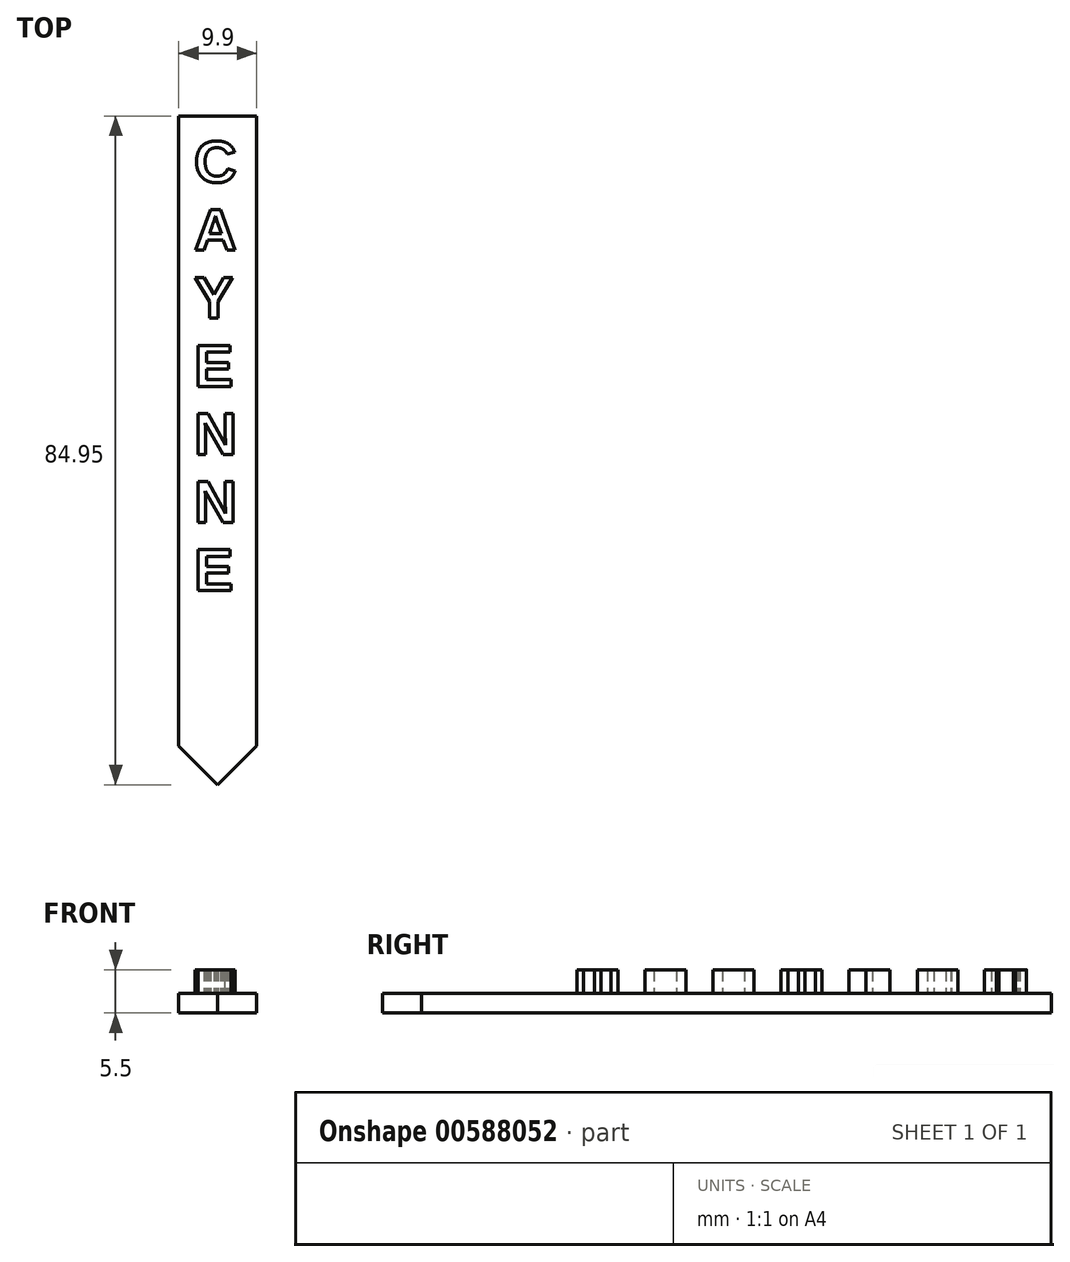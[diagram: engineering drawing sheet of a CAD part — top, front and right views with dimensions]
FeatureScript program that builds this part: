
annotation { "Feature Type Name" : "Feature", "Feature Type Description" : "" }
export const myFeature = defineFeature(function(context is Context, id is Id, definition is map)
    precondition{}
    {
        {
            var Q0;
            Q0=qCreatedBy(makeId("Top.planeOp"),FACE);
            var sketch = newSketch(context, id + "F0", { "sketchPlane" : qUnion([Q0])});
            skLineSegment(sketch, "E0", {"start": v(0, 0) * mm, "end": v(4.95, 4.95) * mm});
            skLineSegment(sketch, "E1", {"start": v(0, 0) * mm, "end": v(-4.95, 4.95) * mm});
            skPoint(sketch, "E2.end.orphan", {"position": v(-3.53, 0) * mm});
            skPoint(sketch, "E3.end.orphan", {"position": v(4.95, 0) * mm});
            skLineSegment(sketch, "E4", {"start": v(4.95, 4.95) * mm, "end": v(4.95, 84.95) * mm});
            skLineSegment(sketch, "E5", {"start": v(-4.95, 4.95) * mm, "end": v(-4.95, 84.95) * mm});
            skLineSegment(sketch, "E6", {"start": v(-4.95, 84.95) * mm, "end": v(4.95, 84.95) * mm});
            skSolve(sketch);
        }
        {
            var Q0;
            Q0=qSketchRegion(id+"F0",true);
            extrude(context, id + "F1", {"entities" : qUnion([Q0]), "depth" : 2.5 * mm, "offsetDistance" : 25 * mm});
        }
        {
            var Q0;
            Q0=makeQuery(id+"F1.opExtrude","CAP_FACE",FACE,{"disambiguationData":[OSD([sQuery(id+"F0.wireOp",EDGE,"E0"),sQuery(id+"F0.wireOp",EDGE,"E1"),sQuery(id+"F0.wireOp",EDGE,"E4"),sQuery(id+"F0.wireOp",EDGE,"E5"),sQuery(id+"F0.wireOp",EDGE,"E6")])],"isStart":false});
            var sketch = newSketch(context, id + "F2", { "sketchPlane" : qUnion([Q0])});
            skText(sketch, "E7", { "text": "C\nA\nY\nE\nN\nN\nE", "fontName": "Arimo-Bold.ttf"});
            const initialGuessF2  = {"E7": [-0.003, 0.07654, 1, 0, 0.00541]};
            skSetInitialGuess(sketch, initialGuessF2);
            skSolve(sketch);
        }
        {
            var Q0;
            Q0=qSketchRegion(id+"F2",true);
            extrude(context, id + "F3", {"entities" : qUnion([Q0]), "operationType" : NewBodyOperationType.ADD, "depth" : 3 * mm, "offsetDistance" : 25 * mm});
        }
    });
